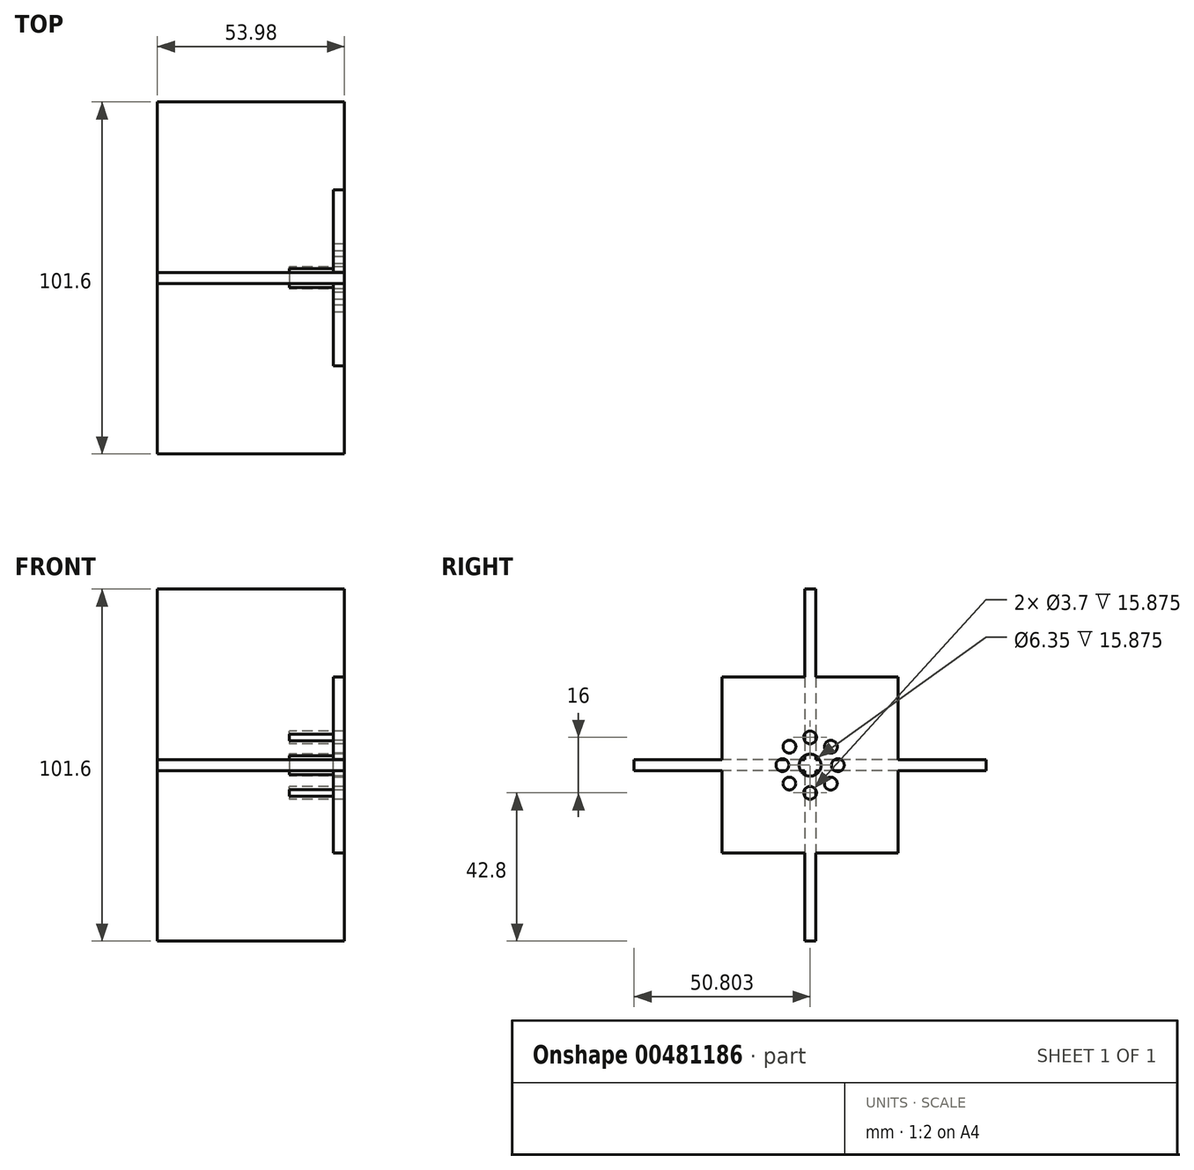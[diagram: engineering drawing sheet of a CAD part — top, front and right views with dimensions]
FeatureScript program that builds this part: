
annotation { "Feature Type Name" : "Feature", "Feature Type Description" : "" }
export const myFeature = defineFeature(function(context is Context, id is Id, definition is map)
    precondition{}
    {
        {
            var Q0;
            Q0=qCreatedBy(makeId("Front.planeOp"),FACE);
            var sketch = newSketch(context, id + "F0", { "sketchPlane" : qUnion([Q0])});
            skLineSegment(sketch, "E0.bottom", {"start": v(-25.4, 50.8) * mm, "end": v(25.4, 50.8) * mm});
            skLineSegment(sketch, "E0.top", {"start": v(-25.4, -50.8) * mm, "end": v(25.4, -50.8) * mm});
            skLineSegment(sketch, "E0.left", {"start": v(-25.4, 50.8) * mm, "end": v(-25.4, -50.8) * mm});
            skLineSegment(sketch, "E0.right", {"start": v(25.4, 50.8) * mm, "end": v(25.4, -50.8) * mm});
            skPoint(sketch, "E1", {"position": v(0, 0) * mm});
            skPoint(sketch, "E1.positionSnap0", {"position": v(-25.4, 0) * mm});
            skPoint(sketch, "E1.positionSnap1", {"position": v(0, 50.8) * mm});
            skSolve(sketch);
        }
        {
            var Q0;
            Q0=makeQuery(id+"F0.imprint","IMPRINT",FACE,{"disambiguationData":[TD([[makeQuery(id+"F0.imprint","IMPRINT",EDGE,{"derivedFrom":sQuery(id+"F0.wireOp",EDGE,"E0.bottom")}),-1.0]])]});
            extrude(context, id + "F1", {"entities" : qUnion([Q0]), "depth" : 3.17 * mm});
        }
        {
            var Q0;
            Q0=qCreatedBy(makeId("Top.planeOp"),FACE);
            var sketch = newSketch(context, id + "F2", { "sketchPlane" : qUnion([Q0])});
            skLineSegment(sketch, "E2.bottom", {"start": v(-25.4, 49.21) * mm, "end": v(25.4, 49.21) * mm});
            skLineSegment(sketch, "E2.top", {"start": v(-25.4, -52.39) * mm, "end": v(25.4, -52.39) * mm});
            skLineSegment(sketch, "E2.left", {"start": v(-25.4, 49.21) * mm, "end": v(-25.4, -52.39) * mm});
            skLineSegment(sketch, "E2.right", {"start": v(25.4, 49.21) * mm, "end": v(25.4, -52.39) * mm});
            skPoint(sketch, "E3", {"position": v(0, -1.59) * mm});
            skPoint(sketch, "E3.positionSnap0", {"position": v(-25.4, -1.59) * mm});
            skPoint(sketch, "E3.positionSnap1", {"position": v(0, 49.21) * mm});
            skSolve(sketch);
        }
        {
            var Q0;
            Q0=makeQuery(id+"F2.imprint","IMPRINT",FACE,{"disambiguationData":[TD([[makeQuery(id+"F2.imprint","IMPRINT",EDGE,{"derivedFrom":sQuery(id+"F2.wireOp",EDGE,"E2.bottom")}),-1.0]])]});
            extrude(context, id + "F3", {"entities" : qUnion([Q0]), "operationType" : NewBodyOperationType.ADD, "depth" : 1.59 * mm});
        }
        {
            var Q0;
            Q0 = qSketchRegion(id + "F2", true);
            extrude(context, id + "F4", {"entities" : qUnion([Q0]), "operationType" : NewBodyOperationType.ADD, "oppositeDirection" : true, "depth" : 1.59 * mm});
        }
        {
            var Q0;
            {var subQ0=sQuery(id+"F2.wireOp",EDGE,"E2.right");Q0=makeQuery(id+"Ffu5bWNMgdVv4E8_1.boolean.opBoolean","MERGE",FACE,{"derivedFrom":[makeQuery(id+"F4.boolean.opBoolean","MERGE",FACE,{"derivedFrom":[makeQuery(id+"F3.boolean.opBoolean","MERGE",FACE,{"derivedFrom":[makeQuery(id+"F1.opExtrude","SWEPT_FACE",FACE,{"disambiguationData":[OSD([sQuery(id+"F0.wireOp",EDGE,"E0.right")])]}),makeQuery(id+"F3.opExtrude","SWEPT_FACE",FACE,{"disambiguationData":[OSD([subQ0])]})]}),makeQuery(id+"F4.opExtrude","SWEPT_FACE",FACE,{"disambiguationData":[OSD([subQ0])]})]}),makeQuery(id+"Ffu5bWNMgdVv4E8_1.opExtrude","CAP_FACE",FACE,{"disambiguationData":[OSD([sQuery(id+"FQvqLoLtU5Hr7tz_1.wireOp",EDGE,"tEkSdxkC-TZZQ-tEbt-xZHG-kROGwQniLN7B.bottom"),sQuery(id+"FQvqLoLtU5Hr7tz_1.wireOp",EDGE,"tEkSdxkC-TZZQ-tEbt-xZHG-kROGwQniLN7B.top"),sQuery(id+"FQvqLoLtU5Hr7tz_1.wireOp",EDGE,"tEkSdxkC-TZZQ-tEbt-xZHG-kROGwQniLN7B.left"),sQuery(id+"FQvqLoLtU5Hr7tz_1.wireOp",EDGE,"tEkSdxkC-TZZQ-tEbt-xZHG-kROGwQniLN7B.right")])],"isStart":true})]});}
            var sketch = newSketch(context, id + "F5", { "sketchPlane" : qUnion([Q0])});
            skPoint(sketch, "E4", {"position": v(-1.59, 0) * mm});
            skCircle(sketch, "E5", {"center": v(-1.59, 0) * mm, "radius": 3.18 * mm});
            skLineSegment(sketch, "E6.bottom", {"start": v(-26.99, 25.4) * mm, "end": v(23.81, 25.4) * mm});
            skLineSegment(sketch, "E6.top", {"start": v(-26.99, -25.4) * mm, "end": v(23.81, -25.4) * mm});
            skLineSegment(sketch, "E6.left", {"start": v(-26.99, 25.4) * mm, "end": v(-26.99, -25.4) * mm});
            skLineSegment(sketch, "E6.right", {"start": v(23.81, 25.4) * mm, "end": v(23.81, -25.4) * mm});
            skPoint(sketch, "E7.positionSnap0", {"position": v(-26.99, 0) * mm});
            skPoint(sketch, "E7.positionSnap1", {"position": v(-1.59, 25.4) * mm});
            skCircle(sketch, "E8", {"center": v(-1.59, 8) * mm, "radius": 1.85 * mm});
            skCircle(sketch, "E9", {"center": v(-1.59, -8) * mm, "radius": 1.85 * mm});
            skCircle(sketch, "E10", {"center": v(6.41, 0) * mm, "radius": 1.85 * mm});
            skCircle(sketch, "E11", {"center": v(-9.59, 0) * mm, "radius": 1.85 * mm});
            skCircle(sketch, "E12", {"center": v(-7.55, 5.34) * mm, "radius": 1.85 * mm});
            skCircle(sketch, "E13", {"center": v(-7.58, -5.3) * mm, "radius": 1.85 * mm});
            skCircle(sketch, "E14", {"center": v(4.37, -5.34) * mm, "radius": 1.85 * mm});
            skCircle(sketch, "E15", {"center": v(4.4, 5.3) * mm, "radius": 1.85 * mm});
            skLineSegment(sketch, "E16", {"start": v(-7.55, 5.34) * mm, "end": v(4.37, -5.34) * mm, "construction": true});
            skLineSegment(sketch, "E17", {"start": v(-7.58, -5.3) * mm, "end": v(4.4, 5.3) * mm, "construction": true});
            skSolve(sketch);
        }
        {
            var Q0;
            Q0=makeQuery(id+"F5.imprint","IMPRINT",FACE,{"disambiguationData":[TD([[makeQuery(id+"F5.imprint","IMPRINT",EDGE,{"derivedFrom":sQuery(id+"F5.wireOp",EDGE,"E12")}),-1.0]])]});
            var Q1;
            Q1=makeQuery(id+"F5.imprint","IMPRINT",FACE,{"disambiguationData":[TD([[makeQuery(id+"F5.imprint","IMPRINT",EDGE,{"derivedFrom":sQuery(id+"F5.wireOp",EDGE,"E15")}),-1.0]])]});
            var Q2;
            Q2=makeQuery(id+"F5.imprint","IMPRINT",FACE,{"disambiguationData":[TD([[makeQuery(id+"F5.imprint","IMPRINT",EDGE,{"derivedFrom":sQuery(id+"F5.wireOp",EDGE,"E14")}),-1.0]])]});
            var Q3;
            Q3=makeQuery(id+"F5.imprint","IMPRINT",FACE,{"disambiguationData":[TD([[makeQuery(id+"F5.imprint","IMPRINT",EDGE,{"derivedFrom":sQuery(id+"F5.wireOp",EDGE,"E13")}),-1.0]])]});
            var Q4;
            {var subQ0=sQuery(id+"F5.wireOp",EDGE,"E5");var subQ1=sQuery(id+"F2.wireOp",EDGE,"E2.top");var subQ2=makeQuery(id+"F3.opExtrude","SWEPT_FACE",FACE,{"disambiguationData":[OSD([subQ1])]});var subQ3=sQuery(id+"F2.wireOp",EDGE,"E2.right");var subQ10=makeQuery(id+"F3.boolean.opBoolean","SPLIT",EDGE,{"disambiguationData":[TD([subQ2])],"derivedFrom":makeQuery(id+"F3.opExtrude","CAP_EDGE",EDGE,{"disambiguationData":[OSD([subQ3])],"isStart":false})});var subQ11=makeQuery(id+"F5.imprint","INTERSECT",VERTEX,{"derivedFrom":[subQ10,subQ0]});Q4=makeQuery(id+"F5.imprint","IMPRINT",FACE,{"disambiguationData":[TD([[makeQuery(id+"F5.imprint","IMPRINT",EDGE,{"disambiguationData":[TD([[subQ11,-1.0]])],"derivedFrom":subQ0}),-1.0]])]});}
            var Q5;
            {var subQ0=sQuery(id+"F5.wireOp",EDGE,"E5");var subQ1=sQuery(id+"F0.wireOp",EDGE,"E0.right");var subQ4=sQuery(id+"F0.wireOp",EDGE,"E0.bottom");var subQ8=makeQuery(id+"F1.opExtrude","SWEPT_FACE",FACE,{"disambiguationData":[OSD([subQ4])]});var subQ10=makeQuery(id+"F3.boolean.opBoolean","SPLIT",EDGE,{"disambiguationData":[TD([subQ8])],"derivedFrom":makeQuery(id+"F1.opExtrude","CAP_EDGE",EDGE,{"disambiguationData":[OSD([subQ1])],"isStart":true})});var subQ11=makeQuery(id+"F5.imprint","INTERSECT",VERTEX,{"derivedFrom":[subQ10,subQ0]});Q5=makeQuery(id+"F5.imprint","IMPRINT",FACE,{"disambiguationData":[TD([[makeQuery(id+"F5.imprint","IMPRINT",EDGE,{"disambiguationData":[TD([[subQ11,-1.0]])],"derivedFrom":subQ0}),-1.0]])]});}
            var Q6;
            {var subQ0=sQuery(id+"F5.wireOp",EDGE,"E5");var subQ1=sQuery(id+"F2.wireOp",EDGE,"E2.bottom");var subQ2=makeQuery(id+"F3.opExtrude","SWEPT_FACE",FACE,{"disambiguationData":[OSD([subQ1])]});var subQ5=sQuery(id+"F2.wireOp",EDGE,"E2.right");var subQ10=makeQuery(id+"F3.boolean.opBoolean","SPLIT",EDGE,{"disambiguationData":[TD([subQ2])],"derivedFrom":makeQuery(id+"F3.opExtrude","CAP_EDGE",EDGE,{"disambiguationData":[OSD([subQ5])],"isStart":false})});var subQ11=makeQuery(id+"F5.imprint","INTERSECT",VERTEX,{"derivedFrom":[subQ10,subQ0]});Q6=makeQuery(id+"F5.imprint","IMPRINT",FACE,{"disambiguationData":[TD([[makeQuery(id+"F5.imprint","IMPRINT",EDGE,{"disambiguationData":[TD([[subQ11,1.0]])],"derivedFrom":subQ0}),-1.0]])]});}
            var Q7;
            {var subQ0=sQuery(id+"F5.wireOp",EDGE,"E5");var subQ3=sQuery(id+"F0.wireOp",EDGE,"E0.right");var subQ5=sQuery(id+"F0.wireOp",EDGE,"E0.top");var subQ8=makeQuery(id+"F1.opExtrude","SWEPT_FACE",FACE,{"disambiguationData":[OSD([subQ5])]});var subQ10=makeQuery(id+"F3.boolean.opBoolean","SPLIT",EDGE,{"disambiguationData":[TD([subQ8])],"derivedFrom":makeQuery(id+"F1.opExtrude","CAP_EDGE",EDGE,{"disambiguationData":[OSD([subQ3])],"isStart":false})});var subQ11=makeQuery(id+"F5.imprint","INTERSECT",VERTEX,{"derivedFrom":[subQ10,subQ0]});Q7=makeQuery(id+"F5.imprint","IMPRINT",FACE,{"disambiguationData":[TD([[makeQuery(id+"F5.imprint","IMPRINT",EDGE,{"disambiguationData":[TD([[subQ11,-1.0]])],"derivedFrom":subQ0}),-1.0]])]});}
            var Q8;
            {var subQ0=sQuery(id+"F5.wireOp",EDGE,"E6.left");var subQ1=sQuery(id+"F2.wireOp",EDGE,"E2.top");var subQ2=makeQuery(id+"F3.opExtrude","SWEPT_FACE",FACE,{"disambiguationData":[OSD([subQ1])]});var subQ3=sQuery(id+"F2.wireOp",EDGE,"E2.right");var subQ10=makeQuery(id+"F3.boolean.opBoolean","SPLIT",EDGE,{"disambiguationData":[TD([subQ2])],"derivedFrom":makeQuery(id+"F3.opExtrude","CAP_EDGE",EDGE,{"disambiguationData":[OSD([subQ3])],"isStart":false})});var subQ11=makeQuery(id+"F5.imprint","INTERSECT",VERTEX,{"derivedFrom":[subQ10,subQ0]});Q8=makeQuery(id+"F5.imprint","IMPRINT",FACE,{"disambiguationData":[TD([[makeQuery(id+"F5.imprint","IMPRINT",EDGE,{"disambiguationData":[TD([[subQ11,-1.0]])],"derivedFrom":subQ0}),1.0]])]});}
            var Q9;
            {var subQ0=sQuery(id+"F5.wireOp",EDGE,"E6.bottom");var subQ1=sQuery(id+"F0.wireOp",EDGE,"E0.right");var subQ4=sQuery(id+"F0.wireOp",EDGE,"E0.bottom");var subQ8=makeQuery(id+"F1.opExtrude","SWEPT_FACE",FACE,{"disambiguationData":[OSD([subQ4])]});var subQ10=makeQuery(id+"F3.boolean.opBoolean","SPLIT",EDGE,{"disambiguationData":[TD([subQ8])],"derivedFrom":makeQuery(id+"F1.opExtrude","CAP_EDGE",EDGE,{"disambiguationData":[OSD([subQ1])],"isStart":false})});var subQ11=makeQuery(id+"F5.imprint","INTERSECT",VERTEX,{"derivedFrom":[subQ10,subQ0]});Q9=makeQuery(id+"F5.imprint","IMPRINT",FACE,{"disambiguationData":[TD([[makeQuery(id+"F5.imprint","IMPRINT",EDGE,{"disambiguationData":[TD([[subQ11,-1.0]])],"derivedFrom":subQ0}),-1.0]])]});}
            var Q10;
            {var subQ0=sQuery(id+"F5.wireOp",EDGE,"E6.right");var subQ1=sQuery(id+"F2.wireOp",EDGE,"E2.bottom");var subQ2=makeQuery(id+"F3.opExtrude","SWEPT_FACE",FACE,{"disambiguationData":[OSD([subQ1])]});var subQ5=sQuery(id+"F2.wireOp",EDGE,"E2.right");var subQ10=makeQuery(id+"F3.boolean.opBoolean","SPLIT",EDGE,{"disambiguationData":[TD([subQ2])],"derivedFrom":makeQuery(id+"F3.opExtrude","CAP_EDGE",EDGE,{"disambiguationData":[OSD([subQ5])],"isStart":false})});var subQ11=makeQuery(id+"F5.imprint","INTERSECT",VERTEX,{"derivedFrom":[subQ10,subQ0]});Q10=makeQuery(id+"F5.imprint","IMPRINT",FACE,{"disambiguationData":[TD([[makeQuery(id+"F5.imprint","IMPRINT",EDGE,{"disambiguationData":[TD([[subQ11,-1.0]])],"derivedFrom":subQ0}),-1.0]])]});}
            var Q11;
            {var subQ0=sQuery(id+"F5.wireOp",EDGE,"E6.top");var subQ3=sQuery(id+"F0.wireOp",EDGE,"E0.right");var subQ5=sQuery(id+"F0.wireOp",EDGE,"E0.top");var subQ8=makeQuery(id+"F1.opExtrude","SWEPT_FACE",FACE,{"disambiguationData":[OSD([subQ5])]});var subQ10=makeQuery(id+"F3.boolean.opBoolean","SPLIT",EDGE,{"disambiguationData":[TD([subQ8])],"derivedFrom":makeQuery(id+"F1.opExtrude","CAP_EDGE",EDGE,{"disambiguationData":[OSD([subQ3])],"isStart":false})});var subQ11=makeQuery(id+"F5.imprint","INTERSECT",VERTEX,{"derivedFrom":[subQ10,subQ0]});Q11=makeQuery(id+"F5.imprint","IMPRINT",FACE,{"disambiguationData":[TD([[makeQuery(id+"F5.imprint","IMPRINT",EDGE,{"disambiguationData":[TD([[subQ11,-1.0]])],"derivedFrom":subQ0}),1.0]])]});}
            extrude(context, id + "F6", {"entities" : qUnion([Q0, Q1, Q2, Q3, Q4, Q5, Q6, Q7, Q8, Q9, Q10, Q11]), "operationType" : NewBodyOperationType.ADD, "depth" : 3.17 * mm});
        }
        {
            var Q0;
            {var subQ0=sQuery(id+"F5.wireOp",EDGE,"E11");var subQ1=sQuery(id+"F2.wireOp",EDGE,"E2.top");var subQ2=makeQuery(id+"F3.opExtrude","SWEPT_FACE",FACE,{"disambiguationData":[OSD([subQ1])]});var subQ3=sQuery(id+"F2.wireOp",EDGE,"E2.right");var subQ10=makeQuery(id+"F3.boolean.opBoolean","SPLIT",EDGE,{"disambiguationData":[TD([subQ2])],"derivedFrom":makeQuery(id+"F3.opExtrude","CAP_EDGE",EDGE,{"disambiguationData":[OSD([subQ3])],"isStart":false})});var subQ11=makeQuery(id+"F5.imprint","INTERSECT",VERTEX,{"disambiguationData":[OD(0.0)],"derivedFrom":[subQ10,subQ0]});Q0=makeQuery(id+"F5.imprint","IMPRINT",FACE,{"disambiguationData":[TD([[makeQuery(id+"F5.imprint","IMPRINT",EDGE,{"disambiguationData":[TD([[subQ11,-1.0]])],"derivedFrom":subQ0}),1.0]])]});}
            var Q1;
            Q1=makeQuery(id+"F5.imprint","IMPRINT",FACE,{"disambiguationData":[TD([[makeQuery(id+"F5.imprint","IMPRINT",EDGE,{"derivedFrom":sQuery(id+"F5.wireOp",EDGE,"E12")}),1.0]])]});
            var Q2;
            {var subQ0=sQuery(id+"F5.wireOp",EDGE,"E8");var subQ1=sQuery(id+"F0.wireOp",EDGE,"E0.right");var subQ4=sQuery(id+"F0.wireOp",EDGE,"E0.bottom");var subQ8=makeQuery(id+"F1.opExtrude","SWEPT_FACE",FACE,{"disambiguationData":[OSD([subQ4])]});var subQ10=makeQuery(id+"F3.boolean.opBoolean","SPLIT",EDGE,{"disambiguationData":[TD([subQ8])],"derivedFrom":makeQuery(id+"F1.opExtrude","CAP_EDGE",EDGE,{"disambiguationData":[OSD([subQ1])],"isStart":false})});var subQ11=makeQuery(id+"F5.imprint","INTERSECT",VERTEX,{"disambiguationData":[OD(0.0)],"derivedFrom":[subQ10,subQ0]});Q2=makeQuery(id+"F5.imprint","IMPRINT",FACE,{"disambiguationData":[TD([[makeQuery(id+"F5.imprint","IMPRINT",EDGE,{"disambiguationData":[TD([[subQ11,1.0]])],"derivedFrom":subQ0}),1.0]])]});}
            var Q3;
            Q3=makeQuery(id+"F5.imprint","IMPRINT",FACE,{"disambiguationData":[TD([[makeQuery(id+"F5.imprint","IMPRINT",EDGE,{"derivedFrom":sQuery(id+"F5.wireOp",EDGE,"E15")}),1.0]])]});
            var Q4;
            {var subQ0=sQuery(id+"F5.wireOp",EDGE,"E10");var subQ1=sQuery(id+"F2.wireOp",EDGE,"E2.bottom");var subQ2=makeQuery(id+"F3.opExtrude","SWEPT_FACE",FACE,{"disambiguationData":[OSD([subQ1])]});var subQ5=sQuery(id+"F2.wireOp",EDGE,"E2.right");var subQ10=makeQuery(id+"F3.boolean.opBoolean","SPLIT",EDGE,{"disambiguationData":[TD([subQ2])],"derivedFrom":makeQuery(id+"F3.opExtrude","CAP_EDGE",EDGE,{"disambiguationData":[OSD([subQ5])],"isStart":false})});var subQ11=makeQuery(id+"F5.imprint","INTERSECT",VERTEX,{"disambiguationData":[OD(0.0)],"derivedFrom":[subQ10,subQ0]});Q4=makeQuery(id+"F5.imprint","IMPRINT",FACE,{"disambiguationData":[TD([[makeQuery(id+"F5.imprint","IMPRINT",EDGE,{"disambiguationData":[TD([[subQ11,-1.0]])],"derivedFrom":subQ0}),1.0]])]});}
            var Q5;
            Q5=makeQuery(id+"F5.imprint","IMPRINT",FACE,{"disambiguationData":[TD([[makeQuery(id+"F5.imprint","IMPRINT",EDGE,{"derivedFrom":sQuery(id+"F5.wireOp",EDGE,"E14")}),1.0]])]});
            var Q6;
            {var subQ0=sQuery(id+"F5.wireOp",EDGE,"E9");var subQ3=sQuery(id+"F0.wireOp",EDGE,"E0.right");var subQ5=sQuery(id+"F0.wireOp",EDGE,"E0.top");var subQ8=makeQuery(id+"F1.opExtrude","SWEPT_FACE",FACE,{"disambiguationData":[OSD([subQ5])]});var subQ10=makeQuery(id+"F3.boolean.opBoolean","SPLIT",EDGE,{"disambiguationData":[TD([subQ8])],"derivedFrom":makeQuery(id+"F1.opExtrude","CAP_EDGE",EDGE,{"disambiguationData":[OSD([subQ3])],"isStart":false})});var subQ11=makeQuery(id+"F5.imprint","INTERSECT",VERTEX,{"disambiguationData":[OD(0.0)],"derivedFrom":[subQ10,subQ0]});Q6=makeQuery(id+"F5.imprint","IMPRINT",FACE,{"disambiguationData":[TD([[makeQuery(id+"F5.imprint","IMPRINT",EDGE,{"disambiguationData":[TD([[subQ11,1.0]])],"derivedFrom":subQ0}),1.0]])]});}
            var Q7;
            Q7=makeQuery(id+"F5.imprint","IMPRINT",FACE,{"disambiguationData":[TD([[makeQuery(id+"F5.imprint","IMPRINT",EDGE,{"derivedFrom":sQuery(id+"F5.wireOp",EDGE,"E13")}),1.0]])]});
            var Q8;
            {var subQ4=sQuery(id+"F0.wireOp",EDGE,"E0.right");var subQ8=sQuery(id+"F0.wireOp",EDGE,"E0.bottom");var subQ21=sQuery(id+"F5.wireOp",EDGE,"E5");var subQ26=makeQuery(id+"F1.opExtrude","CAP_EDGE",EDGE,{"disambiguationData":[OSD([subQ4])],"isStart":true});var subQ35=makeQuery(id+"F1.opExtrude","SWEPT_FACE",FACE,{"disambiguationData":[OSD([subQ8])]});var subQ36=makeQuery(id+"F3.boolean.opBoolean","SPLIT",EDGE,{"disambiguationData":[TD([subQ35])],"derivedFrom":subQ26});var subQ38=makeQuery(id+"F5.imprint","INTERSECT",VERTEX,{"derivedFrom":[subQ36,subQ21]});Q8=makeQuery(id+"F5.imprint","IMPRINT",FACE,{"disambiguationData":[TD([[makeQuery(id+"F5.imprint","IMPRINT",EDGE,{"disambiguationData":[TD([[subQ38,-1.0]])],"derivedFrom":subQ21}),1.0]])]});}
            var Q9;
            {var subQ0=sQuery(id+"F5.wireOp",EDGE,"E5");var subQ1=sQuery(id+"F0.wireOp",EDGE,"E0.right");var subQ2=sQuery(id+"F0.wireOp",EDGE,"E0.bottom");var subQ9=makeQuery(id+"F3.boolean.opBoolean","SPLIT",EDGE,{"disambiguationData":[TD([makeQuery(id+"F1.opExtrude","SWEPT_FACE",FACE,{"disambiguationData":[OSD([subQ2])]})])],"derivedFrom":makeQuery(id+"F1.opExtrude","CAP_EDGE",EDGE,{"disambiguationData":[OSD([subQ1])],"isStart":false})});var subQ10=makeQuery(id+"F5.imprint","INTERSECT",VERTEX,{"derivedFrom":[subQ9,subQ0]});Q9=makeQuery(id+"F5.imprint","IMPRINT",FACE,{"disambiguationData":[TD([[makeQuery(id+"F5.imprint","IMPRINT",EDGE,{"disambiguationData":[TD([[subQ10,-1.0]])],"derivedFrom":subQ0}),1.0]])]});}
            var Q10;
            {var subQ0=sQuery(id+"F5.wireOp",EDGE,"E5");var subQ1=sQuery(id+"F0.wireOp",EDGE,"E0.right");var subQ2=sQuery(id+"F0.wireOp",EDGE,"E0.bottom");var subQ9=makeQuery(id+"F3.boolean.opBoolean","SPLIT",EDGE,{"disambiguationData":[TD([makeQuery(id+"F1.opExtrude","SWEPT_FACE",FACE,{"disambiguationData":[OSD([subQ2])]})])],"derivedFrom":makeQuery(id+"F1.opExtrude","CAP_EDGE",EDGE,{"disambiguationData":[OSD([subQ1])],"isStart":true})});var subQ10=makeQuery(id+"F5.imprint","INTERSECT",VERTEX,{"derivedFrom":[subQ9,subQ0]});Q10=makeQuery(id+"F5.imprint","IMPRINT",FACE,{"disambiguationData":[TD([[makeQuery(id+"F5.imprint","IMPRINT",EDGE,{"disambiguationData":[TD([[subQ10,1.0]])],"derivedFrom":subQ0}),1.0]])]});}
            var Q11;
            {var subQ0=sQuery(id+"F5.wireOp",EDGE,"E5");var subQ5=sQuery(id+"F0.wireOp",EDGE,"E0.right");var subQ7=sQuery(id+"F0.wireOp",EDGE,"E0.top");var subQ10=makeQuery(id+"F3.boolean.opBoolean","SPLIT",EDGE,{"disambiguationData":[TD([makeQuery(id+"F1.opExtrude","SWEPT_FACE",FACE,{"disambiguationData":[OSD([subQ7])]})])],"derivedFrom":makeQuery(id+"F1.opExtrude","CAP_EDGE",EDGE,{"disambiguationData":[OSD([subQ5])],"isStart":true})});var subQ11=makeQuery(id+"F5.imprint","INTERSECT",VERTEX,{"derivedFrom":[subQ10,subQ0]});Q11=makeQuery(id+"F5.imprint","IMPRINT",FACE,{"disambiguationData":[TD([[makeQuery(id+"F5.imprint","IMPRINT",EDGE,{"disambiguationData":[TD([[subQ11,-1.0]])],"derivedFrom":subQ0}),1.0]])]});}
            var Q12;
            {var subQ0=sQuery(id+"F5.wireOp",EDGE,"E5");var subQ4=sQuery(id+"F0.wireOp",EDGE,"E0.right");var subQ6=sQuery(id+"F0.wireOp",EDGE,"E0.top");var subQ12=makeQuery(id+"F3.boolean.opBoolean","SPLIT",EDGE,{"disambiguationData":[TD([makeQuery(id+"F1.opExtrude","SWEPT_FACE",FACE,{"disambiguationData":[OSD([subQ6])]})])],"derivedFrom":makeQuery(id+"F1.opExtrude","CAP_EDGE",EDGE,{"disambiguationData":[OSD([subQ4])],"isStart":false})});var subQ13=makeQuery(id+"F5.imprint","INTERSECT",VERTEX,{"derivedFrom":[subQ12,subQ0]});Q12=makeQuery(id+"F5.imprint","IMPRINT",FACE,{"disambiguationData":[TD([[makeQuery(id+"F5.imprint","IMPRINT",EDGE,{"disambiguationData":[TD([[subQ13,1.0]])],"derivedFrom":subQ0}),1.0]])]});}
            extrude(context, id + "F7", {"entities" : qUnion([Q0, Q1, Q2, Q3, Q4, Q5, Q6, Q7, Q8, Q9, Q10, Q11, Q12]), "operationType" : NewBodyOperationType.REMOVE, "oppositeDirection" : true, "depth" : 12.7 * mm});
        }
        {
            var Q0;
            {var subQ0=sQuery(id+"F0.wireOp",EDGE,"E0.right");var subQ3=sQuery(id+"F0.wireOp",EDGE,"E0.bottom");var subQ5=sQuery(id+"F2.wireOp",EDGE,"E2.right");Q0=makeQuery(id+"F6.boolean.opBoolean","SPLIT",FACE,{"disambiguationData":[TD([makeQuery(id+"F1.opExtrude","SWEPT_FACE",FACE,{"disambiguationData":[OSD([subQ3])]})])],"derivedFrom":makeQuery(id+"F4.boolean.opBoolean","MERGE",FACE,{"derivedFrom":[makeQuery(id+"F3.boolean.opBoolean","MERGE",FACE,{"derivedFrom":[makeQuery(id+"F1.opExtrude","SWEPT_FACE",FACE,{"disambiguationData":[OSD([subQ0])]}),makeQuery(id+"F3.opExtrude","SWEPT_FACE",FACE,{"disambiguationData":[OSD([subQ5])]})]}),makeQuery(id+"F4.opExtrude","SWEPT_FACE",FACE,{"disambiguationData":[OSD([subQ5])]})]})});}
            var sketch = newSketch(context, id + "F8", { "sketchPlane" : qUnion([Q0])});
            skLineSegment(sketch, "E18.bottom", {"start": v(-3.18, 25.4) * mm, "end": v(0, 25.4) * mm});
            skLineSegment(sketch, "E18.top", {"start": v(-3.18, 50.8) * mm, "end": v(0, 50.8) * mm});
            skLineSegment(sketch, "E18.left", {"start": v(-3.18, 25.4) * mm, "end": v(-3.18, 50.8) * mm});
            skLineSegment(sketch, "E18.right", {"start": v(0, 25.4) * mm, "end": v(0, 50.8) * mm});
            skSolve(sketch);
        }
        {
            var Q0;
            {var subQ0=sQuery(id+"F2.wireOp",EDGE,"E2.top");var subQ1=sQuery(id+"F2.wireOp",EDGE,"E2.right");Q0=makeQuery(id+"F6.boolean.opBoolean","SPLIT",FACE,{"disambiguationData":[TD([makeQuery(id+"F3.opExtrude","SWEPT_FACE",FACE,{"disambiguationData":[OSD([subQ0])]})])],"derivedFrom":makeQuery(id+"F4.boolean.opBoolean","MERGE",FACE,{"derivedFrom":[makeQuery(id+"F3.boolean.opBoolean","MERGE",FACE,{"derivedFrom":[makeQuery(id+"F1.opExtrude","SWEPT_FACE",FACE,{"disambiguationData":[OSD([sQuery(id+"F0.wireOp",EDGE,"E0.right")])]}),makeQuery(id+"F3.opExtrude","SWEPT_FACE",FACE,{"disambiguationData":[OSD([subQ1])]})]}),makeQuery(id+"F4.opExtrude","SWEPT_FACE",FACE,{"disambiguationData":[OSD([subQ1])]})]})});}
            var sketch = newSketch(context, id + "F9", { "sketchPlane" : qUnion([Q0])});
            skLineSegment(sketch, "E19.bottom", {"start": v(-26.99, -1.59) * mm, "end": v(-52.39, -1.59) * mm});
            skLineSegment(sketch, "E19.top", {"start": v(-26.99, 1.59) * mm, "end": v(-52.39, 1.59) * mm});
            skLineSegment(sketch, "E19.left", {"start": v(-26.99, -1.59) * mm, "end": v(-26.99, 1.59) * mm});
            skLineSegment(sketch, "E19.right", {"start": v(-52.39, -1.59) * mm, "end": v(-52.39, 1.59) * mm});
            skSolve(sketch);
        }
        {
            var Q0;
            {var subQ1=sQuery(id+"F0.wireOp",EDGE,"E0.top");var subQ2=sQuery(id+"F0.wireOp",EDGE,"E0.right");var subQ5=sQuery(id+"F2.wireOp",EDGE,"E2.right");Q0=makeQuery(id+"F6.boolean.opBoolean","SPLIT",FACE,{"disambiguationData":[TD([makeQuery(id+"F1.opExtrude","SWEPT_FACE",FACE,{"disambiguationData":[OSD([subQ1])]})])],"derivedFrom":makeQuery(id+"F4.boolean.opBoolean","MERGE",FACE,{"derivedFrom":[makeQuery(id+"F3.boolean.opBoolean","MERGE",FACE,{"derivedFrom":[makeQuery(id+"F1.opExtrude","SWEPT_FACE",FACE,{"disambiguationData":[OSD([subQ2])]}),makeQuery(id+"F3.opExtrude","SWEPT_FACE",FACE,{"disambiguationData":[OSD([subQ5])]})]}),makeQuery(id+"F4.opExtrude","SWEPT_FACE",FACE,{"disambiguationData":[OSD([subQ5])]})]})});}
            var sketch = newSketch(context, id + "F10", { "sketchPlane" : qUnion([Q0])});
            skLineSegment(sketch, "E20.bottom", {"start": v(-3.18, -25.4) * mm, "end": v(0, -25.4) * mm});
            skLineSegment(sketch, "E20.top", {"start": v(-3.18, -50.8) * mm, "end": v(0, -50.8) * mm});
            skLineSegment(sketch, "E20.left", {"start": v(-3.18, -25.4) * mm, "end": v(-3.18, -50.8) * mm});
            skLineSegment(sketch, "E20.right", {"start": v(0, -25.4) * mm, "end": v(0, -50.8) * mm});
            skSolve(sketch);
        }
        {
            var Q0;
            {var subQ0=sQuery(id+"F2.wireOp",EDGE,"E2.right");var subQ3=sQuery(id+"F2.wireOp",EDGE,"E2.bottom");Q0=makeQuery(id+"F6.boolean.opBoolean","SPLIT",FACE,{"disambiguationData":[TD([makeQuery(id+"F3.opExtrude","SWEPT_FACE",FACE,{"disambiguationData":[OSD([subQ3])]})])],"derivedFrom":makeQuery(id+"F4.boolean.opBoolean","MERGE",FACE,{"derivedFrom":[makeQuery(id+"F3.boolean.opBoolean","MERGE",FACE,{"derivedFrom":[makeQuery(id+"F1.opExtrude","SWEPT_FACE",FACE,{"disambiguationData":[OSD([sQuery(id+"F0.wireOp",EDGE,"E0.right")])]}),makeQuery(id+"F3.opExtrude","SWEPT_FACE",FACE,{"disambiguationData":[OSD([subQ0])]})]}),makeQuery(id+"F4.opExtrude","SWEPT_FACE",FACE,{"disambiguationData":[OSD([subQ0])]})]})});}
            var sketch = newSketch(context, id + "F11", { "sketchPlane" : qUnion([Q0])});
            skLineSegment(sketch, "E21.bottom", {"start": v(23.81, 1.59) * mm, "end": v(49.21, 1.59) * mm});
            skLineSegment(sketch, "E21.top", {"start": v(23.81, -1.59) * mm, "end": v(49.21, -1.59) * mm});
            skLineSegment(sketch, "E21.left", {"start": v(23.81, 1.59) * mm, "end": v(23.81, -1.59) * mm});
            skLineSegment(sketch, "E21.right", {"start": v(49.21, 1.59) * mm, "end": v(49.21, -1.59) * mm});
            skSolve(sketch);
        }
        {
            var Q0;
            Q0=makeQuery(id+"F8.imprint","IMPRINT",FACE,{"disambiguationData":[TD([[makeQuery(id+"F8.imprint","IMPRINT",EDGE,{"derivedFrom":sQuery(id+"F8.wireOp",EDGE,"E18.bottom")}),1.0]])]});
            var Q1;
            Q1=makeQuery(id+"F9.imprint","IMPRINT",FACE,{"disambiguationData":[TD([[makeQuery(id+"F9.imprint","IMPRINT",EDGE,{"derivedFrom":sQuery(id+"F9.wireOp",EDGE,"E19.bottom")}),-1.0]])]});
            var Q2;
            Q2=makeQuery(id+"F10.imprint","IMPRINT",FACE,{"disambiguationData":[TD([[makeQuery(id+"F10.imprint","IMPRINT",EDGE,{"derivedFrom":sQuery(id+"F10.wireOp",EDGE,"E20.bottom")}),-1.0]])]});
            var Q3;
            Q3=makeQuery(id+"F11.imprint","IMPRINT",FACE,{"disambiguationData":[TD([[makeQuery(id+"F11.imprint","IMPRINT",EDGE,{"derivedFrom":sQuery(id+"F11.wireOp",EDGE,"E21.bottom")}),1.0]])]});
            extrude(context, id + "F12", {"entities" : qUnion([Q0, Q1, Q2, Q3]), "operationType" : NewBodyOperationType.ADD, "depth" : 3.17 * mm});
        }
    });
